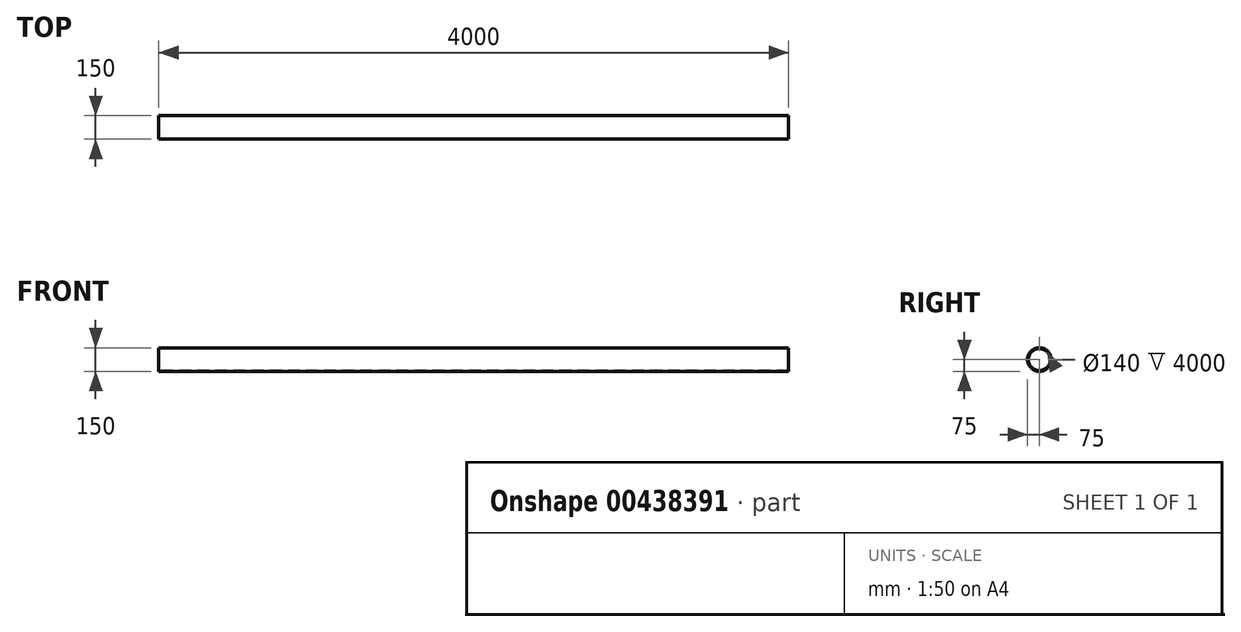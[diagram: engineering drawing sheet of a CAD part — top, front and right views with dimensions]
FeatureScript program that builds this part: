
annotation { "Feature Type Name" : "Feature", "Feature Type Description" : "" }
export const myFeature = defineFeature(function(context is Context, id is Id, definition is map)
    precondition{}
    {
        {
            var Q0;
            Q0=qCreatedBy(makeId("Right.planeOp"),FACE);
            var sketch = newSketch(context, id + "F0", { "sketchPlane" : qUnion([Q0])});
            skCircle(sketch, "E0", {"center": v(0, 0) * mm, "radius": 75 * mm});
            skCircle(sketch, "E1", {"center": v(0, 0) * mm, "radius": 70 * mm});
            skSolve(sketch);
        }
        {
            var Q0;
            Q0=makeQuery(id+"F0.imprint","IMPRINT",FACE,{"disambiguationData":[TD([[makeQuery(id+"F0.imprint","IMPRINT",EDGE,{"derivedFrom":sQuery(id+"F0.wireOp",EDGE,"E0")}),1.0]])]});
            extrude(context, id + "F1", {"entities" : qUnion([Q0]), "depth" : 4000 * mm});
        }
    });
